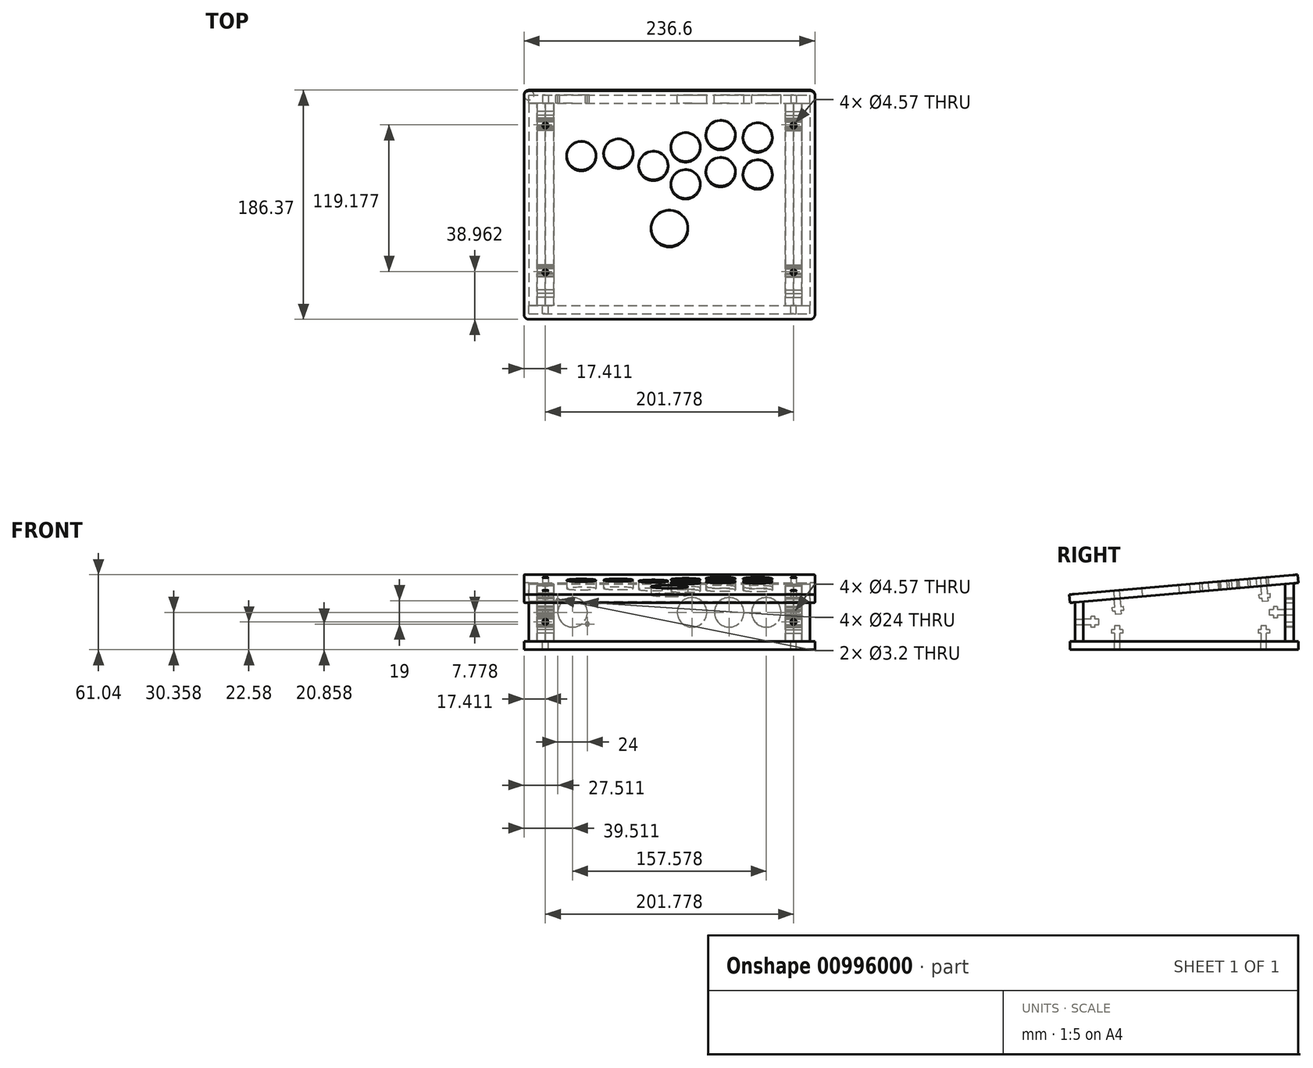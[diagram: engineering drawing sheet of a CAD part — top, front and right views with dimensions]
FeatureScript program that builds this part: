
annotation { "Feature Type Name" : "Feature", "Feature Type Description" : "" }
export const myFeature = defineFeature(function(context is Context, id is Id, definition is map)
    precondition{}
    {
        {
            var Q0;
            Q0=qCreatedBy(makeId("Right.planeOp"),FACE);
            var sketch = newSketch(context, id + "F0", { "sketchPlane" : qUnion([Q0])});
            skLineSegment(sketch, "E0", {"start": v(-88.9, -15.88) * mm, "end": v(88.9, -15.88) * mm});
            skLineSegment(sketch, "E1", {"start": v(88.9, -15.88) * mm, "end": v(88.9, 31.43) * mm});
            skLineSegment(sketch, "E2", {"start": v(88.9, 31.43) * mm, "end": v(-88.9, 15.87) * mm});
            skLineSegment(sketch, "E3", {"start": v(-88.9, 15.88) * mm, "end": v(-88.9, -15.87) * mm});
            skLineSegment(sketch, "E4", {"start": v(82.2, 30.84) * mm, "end": v(82.2, -15.88) * mm});
            skLineSegment(sketch, "E5", {"start": v(-82.2, 16.46) * mm, "end": v(-82.2, -15.88) * mm});
            skLineSegment(sketch, "E6", {"start": v(66.95, -15.88) * mm, "end": v(66.95, -3.17) * mm});
            skLineSegment(sketch, "E7", {"start": v(66.95, -3.17) * mm, "end": v(62.38, -3.17) * mm});
            skLineSegment(sketch, "E8", {"start": v(62.38, -3.17) * mm, "end": v(62.38, -15.88) * mm});
            skLineSegment(sketch, "E9", {"start": v(-52.22, -15.88) * mm, "end": v(-52.22, -3.17) * mm});
            skLineSegment(sketch, "E10", {"start": v(-52.22, -3.17) * mm, "end": v(-56.8, -3.17) * mm});
            skLineSegment(sketch, "E11", {"start": v(-56.8, -3.17) * mm, "end": v(-56.8, -15.88) * mm});
            skLineSegment(sketch, "E12", {"start": v(67.01, 29.52) * mm, "end": v(68.12, 16.86) * mm});
            skLineSegment(sketch, "E13", {"start": v(68.12, 16.86) * mm, "end": v(63.56, 16.47) * mm});
            skLineSegment(sketch, "E14", {"start": v(63.56, 16.47) * mm, "end": v(62.46, 29.12) * mm});
            skLineSegment(sketch, "E15", {"start": v(-52.34, 19.07) * mm, "end": v(-51.23, 6.42) * mm});
            skLineSegment(sketch, "E16", {"start": v(-51.23, 6.42) * mm, "end": v(-55.78, 6.02) * mm});
            skLineSegment(sketch, "E17", {"start": v(-55.78, 6.02) * mm, "end": v(-56.9, 18.68) * mm});
            skLineSegment(sketch, "E18", {"start": v(82.2, 5.5) * mm, "end": v(69.5, 5.5) * mm});
            skLineSegment(sketch, "E19", {"start": v(69.5, 5.5) * mm, "end": v(69.5, 10.06) * mm});
            skLineSegment(sketch, "E20", {"start": v(69.5, 10.06) * mm, "end": v(82.2, 10.06) * mm});
            skLineSegment(sketch, "E21", {"start": v(-82.2, -2.29) * mm, "end": v(-69.5, -2.29) * mm});
            skLineSegment(sketch, "E22", {"start": v(-69.5, -2.29) * mm, "end": v(-69.5, 2.29) * mm});
            skLineSegment(sketch, "E23", {"start": v(-69.5, 2.29) * mm, "end": v(-82.2, 2.29) * mm});
            skPoint(sketch, "E24", {"position": v(-69.5, 0) * mm});
            skPoint(sketch, "E25", {"position": v(69.5, 7.78) * mm});
            skPoint(sketch, "E26", {"position": v(88.9, 7.78) * mm});
            skPoint(sketch, "E27", {"position": v(-88.9, 0) * mm});
            skLineSegment(sketch, "E28.bottom", {"start": v(69.24, -6.22) * mm, "end": v(60.1, -6.22) * mm});
            skLineSegment(sketch, "E28.top", {"start": v(69.24, -9.27) * mm, "end": v(60.1, -9.27) * mm});
            skLineSegment(sketch, "E28.left", {"start": v(69.24, -6.22) * mm, "end": v(69.24, -9.27) * mm});
            skLineSegment(sketch, "E28.right", {"start": v(60.1, -6.22) * mm, "end": v(60.1, -9.27) * mm});
            skLineSegment(sketch, "E29.bottom", {"start": v(-49.94, -6.22) * mm, "end": v(-59.08, -6.22) * mm});
            skLineSegment(sketch, "E29.top", {"start": v(-49.94, -9.27) * mm, "end": v(-59.08, -9.27) * mm});
            skLineSegment(sketch, "E29.left", {"start": v(-49.94, -6.22) * mm, "end": v(-49.94, -9.27) * mm});
            skLineSegment(sketch, "E29.right", {"start": v(-59.08, -6.22) * mm, "end": v(-59.08, -9.27) * mm});
            skLineSegment(sketch, "E30.bottom", {"start": v(-72.54, -4.57) * mm, "end": v(-75.6, -4.57) * mm});
            skLineSegment(sketch, "E30.top", {"start": v(-72.54, 4.57) * mm, "end": v(-75.6, 4.57) * mm});
            skLineSegment(sketch, "E30.left", {"start": v(-72.54, -4.57) * mm, "end": v(-72.54, 4.57) * mm});
            skLineSegment(sketch, "E30.right", {"start": v(-75.6, -4.57) * mm, "end": v(-75.6, 4.57) * mm});
            skLineSegment(sketch, "E31.bottom", {"start": v(-58.33, 8.86) * mm, "end": v(-49.22, 9.66) * mm});
            skLineSegment(sketch, "E31.top", {"start": v(-58.6, 11.9) * mm, "end": v(-49.48, 12.7) * mm});
            skLineSegment(sketch, "E31.left", {"start": v(-58.33, 8.86) * mm, "end": v(-58.6, 11.9) * mm});
            skLineSegment(sketch, "E31.right", {"start": v(-49.22, 9.66) * mm, "end": v(-49.48, 12.7) * mm});
            skLineSegment(sketch, "E32.bottom", {"start": v(61.02, 19.3) * mm, "end": v(70.13, 20.1) * mm});
            skLineSegment(sketch, "E32.top", {"start": v(60.76, 22.34) * mm, "end": v(69.87, 23.14) * mm});
            skLineSegment(sketch, "E32.left", {"start": v(61.02, 19.3) * mm, "end": v(60.76, 22.34) * mm});
            skLineSegment(sketch, "E32.right", {"start": v(70.13, 20.1) * mm, "end": v(69.87, 23.14) * mm});
            skLineSegment(sketch, "E33.bottom", {"start": v(75.6, 12.35) * mm, "end": v(72.54, 12.35) * mm});
            skLineSegment(sketch, "E33.top", {"start": v(75.6, 3.2) * mm, "end": v(72.54, 3.2) * mm});
            skLineSegment(sketch, "E33.left", {"start": v(75.6, 12.35) * mm, "end": v(75.6, 3.2) * mm});
            skLineSegment(sketch, "E33.right", {"start": v(72.54, 12.35) * mm, "end": v(72.54, 3.2) * mm});
            skLineSegment(sketch, "E34", {"start": v(66.95, -3.17) * mm, "end": v(69.24, -6.22) * mm, "construction": true});
            skLineSegment(sketch, "E35", {"start": v(62.38, -3.17) * mm, "end": v(60.1, -6.22) * mm, "construction": true});
            skLineSegment(sketch, "E36", {"start": v(72.54, 3.2) * mm, "end": v(69.5, 5.5) * mm, "construction": true});
            skLineSegment(sketch, "E37", {"start": v(69.5, 10.06) * mm, "end": v(72.54, 12.35) * mm, "construction": true});
            skLineSegment(sketch, "E38", {"start": v(68.12, 16.86) * mm, "end": v(70.13, 20.1) * mm, "construction": true});
            skLineSegment(sketch, "E39", {"start": v(63.56, 16.47) * mm, "end": v(61.02, 19.3) * mm, "construction": true});
            skLineSegment(sketch, "E40", {"start": v(-51.23, 6.42) * mm, "end": v(-49.22, 9.66) * mm, "construction": true});
            skLineSegment(sketch, "E41", {"start": v(-55.78, 6.02) * mm, "end": v(-58.33, 8.86) * mm, "construction": true});
            skLineSegment(sketch, "E42", {"start": v(-69.5, 2.29) * mm, "end": v(-72.54, 4.57) * mm, "construction": true});
            skLineSegment(sketch, "E43", {"start": v(-69.5, -2.29) * mm, "end": v(-72.54, -4.57) * mm, "construction": true});
            skLineSegment(sketch, "E44", {"start": v(-52.22, -3.17) * mm, "end": v(-49.94, -6.22) * mm, "construction": true});
            skLineSegment(sketch, "E45", {"start": v(-56.8, -3.17) * mm, "end": v(-59.08, -6.22) * mm, "construction": true});
            skLineSegment(sketch, "E46", {"start": v(-88.9, 15.88) * mm, "end": v(88.9, 15.87) * mm, "construction": true});
            skSolve(sketch);
        }
        {
            var Q0;
            {var subQ14=sQuery(id+"F0.wireOp",EDGE,"E4");Q0=makeQuery(id+"F0.imprint","IMPRINT",FACE,{"disambiguationData":[TD([[makeQuery(id+"F0.imprint","IMPRINT",EDGE,{"derivedFrom":subQ14}),-1.0]])]});}
            var Q1;
            {var subQ0=sQuery(id+"F0.wireOp",EDGE,"dgdBLiuN-7DTV-gzHf-jHKZ-Ratlxp1D41V1.bottom");Q1=makeQuery(id+"F0.imprint","IMPRINT",FACE,{"disambiguationData":[TD([[makeQuery(id+"F0.imprint","IMPRINT",EDGE,{"derivedFrom":subQ0}),1.0]])]});}
            var Q2;
            {var subQ0=sQuery(id+"F0.wireOp",EDGE,"dgdBLiuN-7DTV-gzHf-jHKZ-Ratlxp1D41V1.top");Q2=makeQuery(id+"F0.imprint","IMPRINT",FACE,{"disambiguationData":[TD([[makeQuery(id+"F0.imprint","IMPRINT",EDGE,{"derivedFrom":subQ0}),-1.0]])]});}
            var Q3;
            {var subQ5=sQuery(id+"F0.wireOp",EDGE,"fHmdqq7Y-QNzh-l0Eo-8w8f-Dmk2epEtvhAU.left");Q3=makeQuery(id+"F0.imprint","IMPRINT",FACE,{"disambiguationData":[TD([[makeQuery(id+"F0.imprint","IMPRINT",EDGE,{"derivedFrom":subQ5}),-1.0]])]});}
            var Q4;
            {var subQ5=sQuery(id+"F0.wireOp",EDGE,"fHmdqq7Y-QNzh-l0Eo-8w8f-Dmk2epEtvhAU.right");Q4=makeQuery(id+"F0.imprint","IMPRINT",FACE,{"disambiguationData":[TD([[makeQuery(id+"F0.imprint","IMPRINT",EDGE,{"derivedFrom":subQ5}),1.0]])]});}
            var Q5;
            {var subQ0=sQuery(id+"F0.wireOp",EDGE,"fHmdqq7Y-QNzh-l0Eo-8w8f-Dmk2epEtvhAU.bottom");var subQ1=sQuery(id+"F0.wireOp",EDGE,"dgdBLiuN-7DTV-gzHf-jHKZ-Ratlxp1D41V1.left");var subQ2=makeQuery(id+"F0.imprint","INTERSECT",VERTEX,{"derivedFrom":[subQ1,subQ0]});Q5=makeQuery(id+"F0.imprint","IMPRINT",FACE,{"disambiguationData":[TD([[makeQuery(id+"F0.imprint","IMPRINT",EDGE,{"disambiguationData":[TD([[subQ2,-1.0]])],"derivedFrom":subQ1}),-1.0]])]});}
            var Q6;
            {var subQ0=sQuery(id+"F0.wireOp",EDGE,"E12");Q6=makeQuery(id+"F0.imprint","IMPRINT",FACE,{"disambiguationData":[TD([[makeQuery(id+"F0.imprint","IMPRINT",EDGE,{"derivedFrom":subQ0}),-1.0]])]});}
            var Q7;
            {var subQ0=sQuery(id+"F0.wireOp",EDGE,"E15");Q7=makeQuery(id+"F0.imprint","IMPRINT",FACE,{"disambiguationData":[TD([[makeQuery(id+"F0.imprint","IMPRINT",EDGE,{"derivedFrom":subQ0}),-1.0]])]});}
            var Q8;
            {var subQ0=sQuery(id+"F0.wireOp",EDGE,"E21");Q8=makeQuery(id+"F0.imprint","IMPRINT",FACE,{"disambiguationData":[TD([[makeQuery(id+"F0.imprint","IMPRINT",EDGE,{"derivedFrom":subQ0}),1.0]])]});}
            var Q9;
            {var subQ0=sQuery(id+"F0.wireOp",EDGE,"E9");Q9=makeQuery(id+"F0.imprint","IMPRINT",FACE,{"disambiguationData":[TD([[makeQuery(id+"F0.imprint","IMPRINT",EDGE,{"derivedFrom":subQ0}),1.0]])]});}
            var Q10;
            {var subQ0=sQuery(id+"F0.wireOp",EDGE,"E6");Q10=makeQuery(id+"F0.imprint","IMPRINT",FACE,{"disambiguationData":[TD([[makeQuery(id+"F0.imprint","IMPRINT",EDGE,{"derivedFrom":subQ0}),1.0]])]});}
            var Q11;
            {var subQ0=sQuery(id+"F0.wireOp",EDGE,"E18");Q11=makeQuery(id+"F0.imprint","IMPRINT",FACE,{"disambiguationData":[TD([[makeQuery(id+"F0.imprint","IMPRINT",EDGE,{"derivedFrom":subQ0}),-1.0]])]});}
            var Q12;
            {var subQ5=sQuery(id+"F0.wireOp",EDGE,"E32.left");Q12=makeQuery(id+"F0.imprint","IMPRINT",FACE,{"disambiguationData":[TD([[makeQuery(id+"F0.imprint","IMPRINT",EDGE,{"derivedFrom":subQ5}),-1.0]])]});}
            var Q13;
            {var subQ5=sQuery(id+"F0.wireOp",EDGE,"E32.right");Q13=makeQuery(id+"F0.imprint","IMPRINT",FACE,{"disambiguationData":[TD([[makeQuery(id+"F0.imprint","IMPRINT",EDGE,{"derivedFrom":subQ5}),1.0]])]});}
            var Q14;
            {var subQ5=sQuery(id+"F0.wireOp",EDGE,"E33.top");Q14=makeQuery(id+"F0.imprint","IMPRINT",FACE,{"disambiguationData":[TD([[makeQuery(id+"F0.imprint","IMPRINT",EDGE,{"derivedFrom":subQ5}),-1.0]])]});}
            var Q15;
            {var subQ5=sQuery(id+"F0.wireOp",EDGE,"E33.bottom");Q15=makeQuery(id+"F0.imprint","IMPRINT",FACE,{"disambiguationData":[TD([[makeQuery(id+"F0.imprint","IMPRINT",EDGE,{"derivedFrom":subQ5}),1.0]])]});}
            var Q16;
            {var subQ5=sQuery(id+"F0.wireOp",EDGE,"E28.left");Q16=makeQuery(id+"F0.imprint","IMPRINT",FACE,{"disambiguationData":[TD([[makeQuery(id+"F0.imprint","IMPRINT",EDGE,{"derivedFrom":subQ5}),-1.0]])]});}
            var Q17;
            {var subQ5=sQuery(id+"F0.wireOp",EDGE,"E28.right");Q17=makeQuery(id+"F0.imprint","IMPRINT",FACE,{"disambiguationData":[TD([[makeQuery(id+"F0.imprint","IMPRINT",EDGE,{"derivedFrom":subQ5}),1.0]])]});}
            var Q18;
            {var subQ5=sQuery(id+"F0.wireOp",EDGE,"E29.left");Q18=makeQuery(id+"F0.imprint","IMPRINT",FACE,{"disambiguationData":[TD([[makeQuery(id+"F0.imprint","IMPRINT",EDGE,{"derivedFrom":subQ5}),-1.0]])]});}
            var Q19;
            {var subQ5=sQuery(id+"F0.wireOp",EDGE,"E29.right");Q19=makeQuery(id+"F0.imprint","IMPRINT",FACE,{"disambiguationData":[TD([[makeQuery(id+"F0.imprint","IMPRINT",EDGE,{"derivedFrom":subQ5}),1.0]])]});}
            var Q20;
            {var subQ5=sQuery(id+"F0.wireOp",EDGE,"E30.bottom");Q20=makeQuery(id+"F0.imprint","IMPRINT",FACE,{"disambiguationData":[TD([[makeQuery(id+"F0.imprint","IMPRINT",EDGE,{"derivedFrom":subQ5}),-1.0]])]});}
            var Q21;
            {var subQ5=sQuery(id+"F0.wireOp",EDGE,"E30.top");Q21=makeQuery(id+"F0.imprint","IMPRINT",FACE,{"disambiguationData":[TD([[makeQuery(id+"F0.imprint","IMPRINT",EDGE,{"derivedFrom":subQ5}),1.0]])]});}
            var Q22;
            {var subQ5=sQuery(id+"F0.wireOp",EDGE,"E31.left");Q22=makeQuery(id+"F0.imprint","IMPRINT",FACE,{"disambiguationData":[TD([[makeQuery(id+"F0.imprint","IMPRINT",EDGE,{"derivedFrom":subQ5}),-1.0]])]});}
            var Q23;
            {var subQ5=sQuery(id+"F0.wireOp",EDGE,"E31.right");Q23=makeQuery(id+"F0.imprint","IMPRINT",FACE,{"disambiguationData":[TD([[makeQuery(id+"F0.imprint","IMPRINT",EDGE,{"derivedFrom":subQ5}),1.0]])]});}
            var Q24;
            {var subQ0=sQuery(id+"F0.wireOp",EDGE,"UAsRLKdk-vdFN-tKB4-pKpE-Und0eIql7xDi");Q24=makeQuery(id+"F0.imprint","IMPRINT",FACE,{"disambiguationData":[TD([[makeQuery(id+"F0.imprint","IMPRINT",EDGE,{"derivedFrom":subQ0}),1.0]])]});}
            extrude(context, id + "F1", {"entities" : qUnion([Q0, Q1, Q2, Q3, Q4, Q5, Q6, Q7, Q8, Q9, Q10, Q11, Q12, Q13, Q14, Q15, Q16, Q17, Q18, Q19, Q20, Q21, Q22, Q23, Q24]), "oppositeDirection" : true, "depth" : 6.7 * mm, "offsetDistance" : 25.4 * mm});
        }
        {
            var Q0;
            {var subQ14=sQuery(id+"F0.wireOp",EDGE,"E4");Q0=makeQuery(id+"F0.imprint","IMPRINT",FACE,{"disambiguationData":[TD([[makeQuery(id+"F0.imprint","IMPRINT",EDGE,{"derivedFrom":subQ14}),-1.0]])]});}
            extrude(context, id + "F2", {"entities" : qUnion([Q0]), "oppositeDirection" : true, "depth" : 6.7 * mm, "offsetDistance" : 25.4 * mm});
        }
        {
            var Q0;
            Q0=makeQuery(id+"F2.opExtrude","SWEPT_BODY",BODY,{"disambiguationData":[OSD([sQuery(id+"F0.wireOp",EDGE,"E0"),sQuery(id+"F0.wireOp",EDGE,"E2"),sQuery(id+"F0.wireOp",EDGE,"E4"),sQuery(id+"F0.wireOp",EDGE,"E5"),sQuery(id+"F0.wireOp",EDGE,"E6"),sQuery(id+"F0.wireOp",EDGE,"E7"),sQuery(id+"F0.wireOp",EDGE,"E8"),sQuery(id+"F0.wireOp",EDGE,"E9"),sQuery(id+"F0.wireOp",EDGE,"E10"),sQuery(id+"F0.wireOp",EDGE,"E11"),sQuery(id+"F0.wireOp",EDGE,"E12"),sQuery(id+"F0.wireOp",EDGE,"E13"),sQuery(id+"F0.wireOp",EDGE,"E14"),sQuery(id+"F0.wireOp",EDGE,"E15"),sQuery(id+"F0.wireOp",EDGE,"E16"),sQuery(id+"F0.wireOp",EDGE,"E17"),sQuery(id+"F0.wireOp",EDGE,"E18"),sQuery(id+"F0.wireOp",EDGE,"E19"),sQuery(id+"F0.wireOp",EDGE,"E20"),sQuery(id+"F0.wireOp",EDGE,"E21"),sQuery(id+"F0.wireOp",EDGE,"E22"),sQuery(id+"F0.wireOp",EDGE,"E23"),sQuery(id+"F0.wireOp",EDGE,"E28.bottom"),sQuery(id+"F0.wireOp",EDGE,"E28.top"),sQuery(id+"F0.wireOp",EDGE,"E28.left"),sQuery(id+"F0.wireOp",EDGE,"E28.right"),sQuery(id+"F0.wireOp",EDGE,"E29.bottom"),sQuery(id+"F0.wireOp",EDGE,"E29.top"),sQuery(id+"F0.wireOp",EDGE,"E29.left"),sQuery(id+"F0.wireOp",EDGE,"E29.right"),sQuery(id+"F0.wireOp",EDGE,"E30.bottom"),sQuery(id+"F0.wireOp",EDGE,"E30.top"),sQuery(id+"F0.wireOp",EDGE,"E30.left"),sQuery(id+"F0.wireOp",EDGE,"E30.right"),sQuery(id+"F0.wireOp",EDGE,"E31.bottom"),sQuery(id+"F0.wireOp",EDGE,"E31.top"),sQuery(id+"F0.wireOp",EDGE,"E31.left"),sQuery(id+"F0.wireOp",EDGE,"E31.right"),sQuery(id+"F0.wireOp",EDGE,"E32.bottom"),sQuery(id+"F0.wireOp",EDGE,"E32.top"),sQuery(id+"F0.wireOp",EDGE,"E32.left"),sQuery(id+"F0.wireOp",EDGE,"E32.right"),sQuery(id+"F0.wireOp",EDGE,"E33.bottom"),sQuery(id+"F0.wireOp",EDGE,"E33.top"),sQuery(id+"F0.wireOp",EDGE,"E33.left"),sQuery(id+"F0.wireOp",EDGE,"E33.right")])]});
            var Q1;
            Q1=makeQuery(id+"F1.opExtrude","SWEPT_EDGE",EDGE,{"disambiguationData":[OSD([sQuery(id+"F0.wireOp",EDGE,"E2"),sQuery(id+"F0.wireOp",EDGE,"E5")])]});
            transform(context, id + "F3", {"entities" : qUnion([Q0]), "transformType" : TransformType.TRANSLATION_ENTITY, "oppositeDirectionEntity" : true, "transformLine" : qUnion([Q1]), "makeCopy" : false});
        }
        {
            var Q0;
            Q0=makeQuery(id+"F2.opExtrude","CAP_FACE",FACE,{"disambiguationData":[OSD([sQuery(id+"F0.wireOp",EDGE,"E0"),sQuery(id+"F0.wireOp",EDGE,"E2"),sQuery(id+"F0.wireOp",EDGE,"E4"),sQuery(id+"F0.wireOp",EDGE,"E5"),sQuery(id+"F0.wireOp",EDGE,"E6"),sQuery(id+"F0.wireOp",EDGE,"E7"),sQuery(id+"F0.wireOp",EDGE,"E8"),sQuery(id+"F0.wireOp",EDGE,"E9"),sQuery(id+"F0.wireOp",EDGE,"E10"),sQuery(id+"F0.wireOp",EDGE,"E11"),sQuery(id+"F0.wireOp",EDGE,"E12"),sQuery(id+"F0.wireOp",EDGE,"E13"),sQuery(id+"F0.wireOp",EDGE,"E14"),sQuery(id+"F0.wireOp",EDGE,"E15"),sQuery(id+"F0.wireOp",EDGE,"E16"),sQuery(id+"F0.wireOp",EDGE,"E17"),sQuery(id+"F0.wireOp",EDGE,"E18"),sQuery(id+"F0.wireOp",EDGE,"E19"),sQuery(id+"F0.wireOp",EDGE,"E20"),sQuery(id+"F0.wireOp",EDGE,"E21"),sQuery(id+"F0.wireOp",EDGE,"E22"),sQuery(id+"F0.wireOp",EDGE,"E23"),sQuery(id+"F0.wireOp",EDGE,"E28.bottom"),sQuery(id+"F0.wireOp",EDGE,"E28.top"),sQuery(id+"F0.wireOp",EDGE,"E28.left"),sQuery(id+"F0.wireOp",EDGE,"E28.right"),sQuery(id+"F0.wireOp",EDGE,"E29.bottom"),sQuery(id+"F0.wireOp",EDGE,"E29.top"),sQuery(id+"F0.wireOp",EDGE,"E29.left"),sQuery(id+"F0.wireOp",EDGE,"E29.right"),sQuery(id+"F0.wireOp",EDGE,"E30.bottom"),sQuery(id+"F0.wireOp",EDGE,"E30.top"),sQuery(id+"F0.wireOp",EDGE,"E30.left"),sQuery(id+"F0.wireOp",EDGE,"E30.right"),sQuery(id+"F0.wireOp",EDGE,"E31.bottom"),sQuery(id+"F0.wireOp",EDGE,"E31.top"),sQuery(id+"F0.wireOp",EDGE,"E31.left"),sQuery(id+"F0.wireOp",EDGE,"E31.right"),sQuery(id+"F0.wireOp",EDGE,"E32.bottom"),sQuery(id+"F0.wireOp",EDGE,"E32.top"),sQuery(id+"F0.wireOp",EDGE,"E32.left"),sQuery(id+"F0.wireOp",EDGE,"E32.right"),sQuery(id+"F0.wireOp",EDGE,"E33.bottom"),sQuery(id+"F0.wireOp",EDGE,"E33.top"),sQuery(id+"F0.wireOp",EDGE,"E33.left"),sQuery(id+"F0.wireOp",EDGE,"E33.right")])],"isStart":false});
            extrude(context, id + "F4", {"entities" : qUnion([Q0]), "depth" : 6.7 * mm, "offsetDistance" : 25.4 * mm});
        }
        {
            var Q0;
            Q0=makeQuery(id+"F1.opExtrude","SWEPT_BODY",BODY,{"disambiguationData":[OSD([sQuery(id+"F0.wireOp",EDGE,"E0"),sQuery(id+"F0.wireOp",EDGE,"E2"),sQuery(id+"F0.wireOp",EDGE,"E4"),sQuery(id+"F0.wireOp",EDGE,"E5"),sQuery(id+"F0.wireOp",EDGE,"dgdBLiuN-7DTV-gzHf-jHKZ-Ratlxp1D41V1.bottom")])]});
            var Q1;
            Q1=makeQuery(id+"F2.opExtrude","SWEPT_BODY",BODY,{"disambiguationData":[OSD([sQuery(id+"F0.wireOp",EDGE,"E0"),sQuery(id+"F0.wireOp",EDGE,"E2"),sQuery(id+"F0.wireOp",EDGE,"E4"),sQuery(id+"F0.wireOp",EDGE,"E5"),sQuery(id+"F0.wireOp",EDGE,"dgdBLiuN-7DTV-gzHf-jHKZ-Ratlxp1D41V1.top"),sQuery(id+"F0.wireOp",EDGE,"dgdBLiuN-7DTV-gzHf-jHKZ-Ratlxp1D41V1.left"),sQuery(id+"F0.wireOp",EDGE,"dgdBLiuN-7DTV-gzHf-jHKZ-Ratlxp1D41V1.right"),sQuery(id+"F0.wireOp",EDGE,"fHmdqq7Y-QNzh-l0Eo-8w8f-Dmk2epEtvhAU.bottom"),sQuery(id+"F0.wireOp",EDGE,"fHmdqq7Y-QNzh-l0Eo-8w8f-Dmk2epEtvhAU.top"),sQuery(id+"F0.wireOp",EDGE,"fHmdqq7Y-QNzh-l0Eo-8w8f-Dmk2epEtvhAU.left"),sQuery(id+"F0.wireOp",EDGE,"fHmdqq7Y-QNzh-l0Eo-8w8f-Dmk2epEtvhAU.right")])]});
            var Q2;
            Q2=makeQuery(id+"F4.opExtrude","SWEPT_BODY",BODY,{"disambiguationData":[OSD([sQuery(id+"F0.wireOp",EDGE,"E0"),sQuery(id+"F0.wireOp",EDGE,"E2"),sQuery(id+"F0.wireOp",EDGE,"E4"),sQuery(id+"F0.wireOp",EDGE,"E5"),sQuery(id+"F0.wireOp",EDGE,"E6"),sQuery(id+"F0.wireOp",EDGE,"E7"),sQuery(id+"F0.wireOp",EDGE,"E8"),sQuery(id+"F0.wireOp",EDGE,"E9"),sQuery(id+"F0.wireOp",EDGE,"E10"),sQuery(id+"F0.wireOp",EDGE,"E11"),sQuery(id+"F0.wireOp",EDGE,"E12"),sQuery(id+"F0.wireOp",EDGE,"E13"),sQuery(id+"F0.wireOp",EDGE,"E14"),sQuery(id+"F0.wireOp",EDGE,"E15"),sQuery(id+"F0.wireOp",EDGE,"E16"),sQuery(id+"F0.wireOp",EDGE,"E17"),sQuery(id+"F0.wireOp",EDGE,"E18"),sQuery(id+"F0.wireOp",EDGE,"E19"),sQuery(id+"F0.wireOp",EDGE,"E20"),sQuery(id+"F0.wireOp",EDGE,"E21"),sQuery(id+"F0.wireOp",EDGE,"E22"),sQuery(id+"F0.wireOp",EDGE,"E23"),sQuery(id+"F0.wireOp",EDGE,"E28.bottom"),sQuery(id+"F0.wireOp",EDGE,"E28.top"),sQuery(id+"F0.wireOp",EDGE,"E28.left"),sQuery(id+"F0.wireOp",EDGE,"E28.right"),sQuery(id+"F0.wireOp",EDGE,"E29.bottom"),sQuery(id+"F0.wireOp",EDGE,"E29.top"),sQuery(id+"F0.wireOp",EDGE,"E29.left"),sQuery(id+"F0.wireOp",EDGE,"E29.right"),sQuery(id+"F0.wireOp",EDGE,"E30.bottom"),sQuery(id+"F0.wireOp",EDGE,"E30.top"),sQuery(id+"F0.wireOp",EDGE,"E30.left"),sQuery(id+"F0.wireOp",EDGE,"E30.right"),sQuery(id+"F0.wireOp",EDGE,"E31.bottom"),sQuery(id+"F0.wireOp",EDGE,"E31.top"),sQuery(id+"F0.wireOp",EDGE,"E31.left"),sQuery(id+"F0.wireOp",EDGE,"E31.right"),sQuery(id+"F0.wireOp",EDGE,"E32.bottom"),sQuery(id+"F0.wireOp",EDGE,"E32.top"),sQuery(id+"F0.wireOp",EDGE,"E32.left"),sQuery(id+"F0.wireOp",EDGE,"E32.right"),sQuery(id+"F0.wireOp",EDGE,"E33.bottom"),sQuery(id+"F0.wireOp",EDGE,"E33.top"),sQuery(id+"F0.wireOp",EDGE,"E33.left"),sQuery(id+"F0.wireOp",EDGE,"E33.right")])]});
            var Q3;
            Q3=qCreatedBy(makeId("Right.planeOp"),FACE);
            mirror(context, id + "F5", {"entities" : qUnion([Q0, Q1, Q2]), "mirrorPlane" : qUnion([Q3])});
        }
        {
            var Q0;
            Q0=makeQuery(id+"F5.opPattern","COPY",BODY,{"derivedFrom":makeQuery(id+"F1.opExtrude","SWEPT_BODY",BODY,{"disambiguationData":[OSD([sQuery(id+"F0.wireOp",EDGE,"E0"),sQuery(id+"F0.wireOp",EDGE,"E2"),sQuery(id+"F0.wireOp",EDGE,"E4"),sQuery(id+"F0.wireOp",EDGE,"E5")])]}),"instanceName":"1"});
            var Q1;
            Q1=makeQuery(id+"F5.opPattern","COPY",BODY,{"derivedFrom":makeQuery(id+"F2.opExtrude","SWEPT_BODY",BODY,{"disambiguationData":[OSD([sQuery(id+"F0.wireOp",EDGE,"E0"),sQuery(id+"F0.wireOp",EDGE,"E2"),sQuery(id+"F0.wireOp",EDGE,"E4"),sQuery(id+"F0.wireOp",EDGE,"E5"),sQuery(id+"F0.wireOp",EDGE,"E6"),sQuery(id+"F0.wireOp",EDGE,"E7"),sQuery(id+"F0.wireOp",EDGE,"E8"),sQuery(id+"F0.wireOp",EDGE,"E9"),sQuery(id+"F0.wireOp",EDGE,"E10"),sQuery(id+"F0.wireOp",EDGE,"E11"),sQuery(id+"F0.wireOp",EDGE,"E12"),sQuery(id+"F0.wireOp",EDGE,"E13"),sQuery(id+"F0.wireOp",EDGE,"E14"),sQuery(id+"F0.wireOp",EDGE,"E15"),sQuery(id+"F0.wireOp",EDGE,"E16"),sQuery(id+"F0.wireOp",EDGE,"E17"),sQuery(id+"F0.wireOp",EDGE,"E18"),sQuery(id+"F0.wireOp",EDGE,"E19"),sQuery(id+"F0.wireOp",EDGE,"E20"),sQuery(id+"F0.wireOp",EDGE,"E21"),sQuery(id+"F0.wireOp",EDGE,"E22"),sQuery(id+"F0.wireOp",EDGE,"E23"),sQuery(id+"F0.wireOp",EDGE,"E28.bottom"),sQuery(id+"F0.wireOp",EDGE,"E28.top"),sQuery(id+"F0.wireOp",EDGE,"E28.left"),sQuery(id+"F0.wireOp",EDGE,"E28.right"),sQuery(id+"F0.wireOp",EDGE,"E29.bottom"),sQuery(id+"F0.wireOp",EDGE,"E29.top"),sQuery(id+"F0.wireOp",EDGE,"E29.left"),sQuery(id+"F0.wireOp",EDGE,"E29.right"),sQuery(id+"F0.wireOp",EDGE,"E30.bottom"),sQuery(id+"F0.wireOp",EDGE,"E30.top"),sQuery(id+"F0.wireOp",EDGE,"E30.left"),sQuery(id+"F0.wireOp",EDGE,"E30.right"),sQuery(id+"F0.wireOp",EDGE,"E31.bottom"),sQuery(id+"F0.wireOp",EDGE,"E31.top"),sQuery(id+"F0.wireOp",EDGE,"E31.left"),sQuery(id+"F0.wireOp",EDGE,"E31.right"),sQuery(id+"F0.wireOp",EDGE,"E32.bottom"),sQuery(id+"F0.wireOp",EDGE,"E32.top"),sQuery(id+"F0.wireOp",EDGE,"E32.left"),sQuery(id+"F0.wireOp",EDGE,"E32.right"),sQuery(id+"F0.wireOp",EDGE,"E33.bottom"),sQuery(id+"F0.wireOp",EDGE,"E33.top"),sQuery(id+"F0.wireOp",EDGE,"E33.left"),sQuery(id+"F0.wireOp",EDGE,"E33.right")])]}),"instanceName":"1"});
            var Q2;
            Q2=makeQuery(id+"F5.opPattern","COPY",BODY,{"derivedFrom":makeQuery(id+"F4.opExtrude","SWEPT_BODY",BODY,{"disambiguationData":[OSD([sQuery(id+"F0.wireOp",EDGE,"E0"),sQuery(id+"F0.wireOp",EDGE,"E2"),sQuery(id+"F0.wireOp",EDGE,"E4"),sQuery(id+"F0.wireOp",EDGE,"E5"),sQuery(id+"F0.wireOp",EDGE,"E6"),sQuery(id+"F0.wireOp",EDGE,"E7"),sQuery(id+"F0.wireOp",EDGE,"E8"),sQuery(id+"F0.wireOp",EDGE,"E9"),sQuery(id+"F0.wireOp",EDGE,"E10"),sQuery(id+"F0.wireOp",EDGE,"E11"),sQuery(id+"F0.wireOp",EDGE,"E12"),sQuery(id+"F0.wireOp",EDGE,"E13"),sQuery(id+"F0.wireOp",EDGE,"E14"),sQuery(id+"F0.wireOp",EDGE,"E15"),sQuery(id+"F0.wireOp",EDGE,"E16"),sQuery(id+"F0.wireOp",EDGE,"E17"),sQuery(id+"F0.wireOp",EDGE,"E18"),sQuery(id+"F0.wireOp",EDGE,"E19"),sQuery(id+"F0.wireOp",EDGE,"E20"),sQuery(id+"F0.wireOp",EDGE,"E21"),sQuery(id+"F0.wireOp",EDGE,"E22"),sQuery(id+"F0.wireOp",EDGE,"E23"),sQuery(id+"F0.wireOp",EDGE,"E28.bottom"),sQuery(id+"F0.wireOp",EDGE,"E28.top"),sQuery(id+"F0.wireOp",EDGE,"E28.left"),sQuery(id+"F0.wireOp",EDGE,"E28.right"),sQuery(id+"F0.wireOp",EDGE,"E29.bottom"),sQuery(id+"F0.wireOp",EDGE,"E29.top"),sQuery(id+"F0.wireOp",EDGE,"E29.left"),sQuery(id+"F0.wireOp",EDGE,"E29.right"),sQuery(id+"F0.wireOp",EDGE,"E30.bottom"),sQuery(id+"F0.wireOp",EDGE,"E30.top"),sQuery(id+"F0.wireOp",EDGE,"E30.left"),sQuery(id+"F0.wireOp",EDGE,"E30.right"),sQuery(id+"F0.wireOp",EDGE,"E31.bottom"),sQuery(id+"F0.wireOp",EDGE,"E31.top"),sQuery(id+"F0.wireOp",EDGE,"E31.left"),sQuery(id+"F0.wireOp",EDGE,"E31.right"),sQuery(id+"F0.wireOp",EDGE,"E32.bottom"),sQuery(id+"F0.wireOp",EDGE,"E32.top"),sQuery(id+"F0.wireOp",EDGE,"E32.left"),sQuery(id+"F0.wireOp",EDGE,"E32.right"),sQuery(id+"F0.wireOp",EDGE,"E33.bottom"),sQuery(id+"F0.wireOp",EDGE,"E33.top"),sQuery(id+"F0.wireOp",EDGE,"E33.left"),sQuery(id+"F0.wireOp",EDGE,"E33.right")])]}),"instanceName":"1"});
            transform(context, id + "F6", {"entities" : qUnion([Q0, Q1, Q2]), "transformType" : TransformType.TRANSLATION_3D, "dx" : -228.6 * mm, "dy" : 0 * mm, "dz" : 0 * mm, "makeCopy" : false});
        }
        {
            var Q0;
            {var subQ0=sQuery(id+"F0.wireOp",EDGE,"E3");Q0=makeQuery(id+"F0.imprint","IMPRINT",FACE,{"disambiguationData":[TD([[makeQuery(id+"F0.imprint","IMPRINT",EDGE,{"derivedFrom":subQ0}),1.0]])]});}
            var Q1;
            {var subQ0=sQuery(id+"F0.wireOp",EDGE,"E1");Q1=makeQuery(id+"F0.imprint","IMPRINT",FACE,{"disambiguationData":[TD([[makeQuery(id+"F0.imprint","IMPRINT",EDGE,{"derivedFrom":subQ0}),1.0]])]});}
            var Q2;
            Q2=makeQuery(id+"F5.opPattern","COPY",FACE,{"derivedFrom":makeQuery(id+"F1.opExtrude","CAP_FACE",FACE,{"disambiguationData":[OSD([sQuery(id+"F0.wireOp",EDGE,"E0"),sQuery(id+"F0.wireOp",EDGE,"E2"),sQuery(id+"F0.wireOp",EDGE,"E4"),sQuery(id+"F0.wireOp",EDGE,"E5")])],"isStart":true}),"instanceName":"1"});
            extrude(context, id + "F7", {"entities" : qUnion([Q0, Q1]), "endBound" : BoundingType.UP_TO_SURFACE, "oppositeDirection" : true, "depth" : 254 * mm, "endBoundEntityFace" : qUnion([Q2]), "offsetDistance" : 25.4 * mm});
        }
        {
            var Q0;
            Q0=makeQuery(id+"F7.opExtrude","SWEPT_FACE",FACE,{"disambiguationData":[OSD([sQuery(id+"F0.wireOp",EDGE,"E5")])]});
            var sketch = newSketch(context, id + "F8", { "sketchPlane" : qUnion([Q0])});
            skCircle(sketch, "E47", {"center": v(215.19, 0) * mm, "radius": 2.29 * mm});
            skCircle(sketch, "E48", {"center": v(13.41, 0) * mm, "radius": 2.29 * mm});
            skSolve(sketch);
        }
        {
            var Q0;
            Q0=makeQuery(id+"F7.opExtrude","SWEPT_FACE",FACE,{"disambiguationData":[OSD([sQuery(id+"F0.wireOp",EDGE,"E4")])]});
            var sketch = newSketch(context, id + "F9", { "sketchPlane" : qUnion([Q0])});
            skCircle(sketch, "E49", {"center": v(-215.19, 7.78) * mm, "radius": 2.29 * mm});
            skCircle(sketch, "E50", {"center": v(-13.41, 7.78) * mm, "radius": 2.29 * mm});
            skSolve(sketch);
        }
        {
            var Q0;
            Q0=qSketchRegion(id+"F8",true);
            extrude(context, id + "F10", {"entities" : qUnion([Q0]), "operationType" : NewBodyOperationType.REMOVE, "endBound" : BoundingType.UP_TO_NEXT, "oppositeDirection" : true, "depth" : 25.4 * mm, "offsetDistance" : 25.4 * mm});
        }
        {
            var Q0;
            Q0=qSketchRegion(id+"F9",true);
            extrude(context, id + "F11", {"entities" : qUnion([Q0]), "operationType" : NewBodyOperationType.REMOVE, "endBound" : BoundingType.UP_TO_NEXT, "oppositeDirection" : true, "depth" : 25.4 * mm, "offsetDistance" : 25.4 * mm});
        }
        {
            var Q0;
            Q0=makeQuery(id+"F1.opExtrude","SWEPT_FACE",FACE,{"disambiguationData":[OSD([sQuery(id+"F0.wireOp",EDGE,"E2")])]});
            var sketch = newSketch(context, id + "F12", { "sketchPlane" : qUnion([Q0])});
            skCircle(sketch, "E51", {"center": v(-114.3, -17.08) * mm, "radius": 15 * mm});
            skCircle(sketch, "E52", {"center": v(-186, 42.07) * mm, "radius": 12 * mm});
            skCircle(sketch, "E53", {"center": v(-155.87, 44.07) * mm, "radius": 12 * mm});
            skCircle(sketch, "E54", {"center": v(-127.38, 34.07) * mm, "radius": 12 * mm});
            skCircle(sketch, "E55", {"center": v(-101.22, 49.17) * mm, "radius": 12 * mm});
            skCircle(sketch, "E56", {"center": v(-72.73, 59.17) * mm, "radius": 12 * mm});
            skCircle(sketch, "E57", {"center": v(-42.6, 57.17) * mm, "radius": 12 * mm});
            skCircle(sketch, "E58", {"center": v(-101.22, 18.97) * mm, "radius": 12 * mm});
            skCircle(sketch, "E59", {"center": v(-72.73, 28.97) * mm, "radius": 12 * mm});
            skCircle(sketch, "E60", {"center": v(-42.6, 26.97) * mm, "radius": 12 * mm});
            skCircle(sketch, "E61", {"center": v(-186, 42.07) * mm, "radius": 13.6 * mm, "construction": true});
            skCircle(sketch, "E62", {"center": v(-155.87, 44.07) * mm, "radius": 13.6 * mm, "construction": true});
            skCircle(sketch, "E63", {"center": v(-127.38, 34.07) * mm, "radius": 13.6 * mm, "construction": true});
            skCircle(sketch, "E64", {"center": v(-101.22, 49.17) * mm, "radius": 13.6 * mm, "construction": true});
            skCircle(sketch, "E65", {"center": v(-72.73, 59.17) * mm, "radius": 13.6 * mm, "construction": true});
            skCircle(sketch, "E66", {"center": v(-42.6, 57.17) * mm, "radius": 13.6 * mm, "construction": true});
            skCircle(sketch, "E67", {"center": v(-101.22, 18.97) * mm, "radius": 13.6 * mm, "construction": true});
            skCircle(sketch, "E68", {"center": v(-72.73, 28.97) * mm, "radius": 13.6 * mm, "construction": true});
            skCircle(sketch, "E69", {"center": v(-42.6, 26.97) * mm, "radius": 13.6 * mm, "construction": true});
            skCircle(sketch, "E70", {"center": v(-114.3, -17.08) * mm, "radius": 16.75 * mm, "construction": true});
            skLineSegment(sketch, "E71", {"start": v(-101.22, 18.97) * mm, "end": v(-72.73, 28.97) * mm, "construction": true});
            skLineSegment(sketch, "E72", {"start": v(-72.73, 28.97) * mm, "end": v(-42.6, 26.97) * mm, "construction": true});
            skLineSegment(sketch, "E73", {"start": v(-72.73, 28.97) * mm, "end": v(-72.73, 59.17) * mm, "construction": true});
            skLineSegment(sketch, "E74", {"start": v(-42.6, 26.97) * mm, "end": v(-42.6, 57.17) * mm, "construction": true});
            skLineSegment(sketch, "E75", {"start": v(-186, 42.07) * mm, "end": v(-155.87, 44.07) * mm, "construction": true});
            skLineSegment(sketch, "E76", {"start": v(-155.87, 44.07) * mm, "end": v(-127.38, 34.07) * mm, "construction": true});
            skLineSegment(sketch, "E77", {"start": v(-127.38, 34.07) * mm, "end": v(-101.22, 18.97) * mm, "construction": true});
            skLineSegment(sketch, "E78", {"start": v(-127.38, 34.07) * mm, "end": v(-101.22, 49.17) * mm, "construction": true});
            skLineSegment(sketch, "E79", {"start": v(-101.22, 49.17) * mm, "end": v(-72.73, 59.17) * mm, "construction": true});
            skLineSegment(sketch, "E80", {"start": v(-72.73, 59.17) * mm, "end": v(-42.6, 57.17) * mm, "construction": true});
            skLineSegment(sketch, "E81", {"start": v(-101.22, 18.97) * mm, "end": v(-101.22, 49.17) * mm, "construction": true});
            skLineSegment(sketch, "E82", {"start": v(-127.38, 34.07) * mm, "end": v(-101.22, 34.07) * mm, "construction": true});
            skPoint(sketch, "E83", {"position": v(-114.3, 34.07) * mm});
            skCircle(sketch, "E84", {"center": v(-215.19, -52.76) * mm, "radius": 2.29 * mm});
            skCircle(sketch, "E85", {"center": v(-13.41, -52.76) * mm, "radius": 2.29 * mm});
            skCircle(sketch, "E86", {"center": v(-13.41, 67.04) * mm, "radius": 2.29 * mm});
            skCircle(sketch, "E87", {"center": v(-215.19, 67.04) * mm, "radius": 2.29 * mm});
            skLineSegment(sketch, "E88", {"start": v(-114.3, 91.3) * mm, "end": v(-114.3, -87.18) * mm, "construction": true});
            skLineSegment(sketch, "E89.bottom", {"start": v(-228.6, 91.3) * mm, "end": v(0, 91.3) * mm});
            skLineSegment(sketch, "E89.top", {"start": v(-228.6, -87.18) * mm, "end": v(0, -87.18) * mm});
            skLineSegment(sketch, "E89.left", {"start": v(-228.6, 91.3) * mm, "end": v(-228.6, -87.18) * mm});
            skLineSegment(sketch, "E89.right", {"start": v(0, 91.3) * mm, "end": v(0, -87.18) * mm});
            skLineSegment(sketch, "E90.0", {"start": v(-232.6, 91.3) * mm, "end": v(-232.6, -87.18) * mm});
            skLineSegment(sketch, "E90.1", {"start": v(-228.6, 95.3) * mm, "end": v(0, 95.3) * mm});
            skLineSegment(sketch, "E90.2", {"start": v(4, 91.3) * mm, "end": v(4, -87.18) * mm});
            skLineSegment(sketch, "E90.3", {"start": v(-228.6, -91.18) * mm, "end": v(0, -91.18) * mm});
            skPoint(sketch, "E91.visualSharp", {"position": v(-232.6, 95.3) * mm});
            skArc(sketch, "E91.filletArc", {"start": v(-228.6, 95.3) * mm, "mid": v(-231.43, 94.13) * mm, "end": v(-232.6, 91.3) * mm});
            skPoint(sketch, "E92.visualSharp", {"position": v(4, 95.3) * mm});
            skArc(sketch, "E92.filletArc", {"start": v(4, 91.3) * mm, "mid": v(2.83, 94.13) * mm, "end": v(0, 95.3) * mm});
            skPoint(sketch, "E93.visualSharp", {"position": v(4, -91.18) * mm});
            skArc(sketch, "E93.filletArc", {"start": v(0, -91.18) * mm, "mid": v(2.83, -90) * mm, "end": v(4, -87.18) * mm});
            skPoint(sketch, "E94.visualSharp", {"position": v(-232.6, -91.18) * mm});
            skArc(sketch, "E94.filletArc", {"start": v(-232.6, -87.18) * mm, "mid": v(-231.43, -90) * mm, "end": v(-228.6, -91.18) * mm});
            skLineSegment(sketch, "E95", {"start": v(-114.3, -17.08) * mm, "end": v(-101.22, 18.97) * mm, "construction": true});
            skSolve(sketch);
        }
        {
            var Q0;
            Q0=qSketchRegion(id+"F12",true);
            var Q1;
            Q1=makeQuery(id+"F12.imprint","IMPRINT",FACE,{"disambiguationData":[TD([[makeQuery(id+"F12.imprint","IMPRINT",EDGE,{"derivedFrom":sQuery(id+"F12.wireOp",EDGE,"E51")}),-1.0]])]});
            var Q2;
            {var subQ1=sQuery(id+"F0.wireOp",EDGE,"E2");Q2=makeQuery(id+"F12.imprint","IMPRINT",FACE,{"disambiguationData":[TD([[makeQuery(id+"F12.imprint","IMPRINT",EDGE,{"derivedFrom":makeQuery(id+"F1.opExtrude","CAP_EDGE",EDGE,{"disambiguationData":[OSD([subQ1])],"isStart":false})}),1.0]])]});}
            extrude(context, id + "F13", {"entities" : qUnion([Q0, Q1, Q2]), "depth" : 6.7 * mm, "offsetDistance" : 25.4 * mm});
        }
        {
            var Q0;
            Q0=makeQuery(id+"F1.opExtrude","SWEPT_FACE",FACE,{"disambiguationData":[OSD([sQuery(id+"F0.wireOp",EDGE,"E0")])]});
            var sketch = newSketch(context, id + "F14", { "sketchPlane" : qUnion([Q0])});
            skLineSegment(sketch, "E96.bottom", {"start": v(0, 88.9) * mm, "end": v(-228.6, 88.9) * mm});
            skLineSegment(sketch, "E96.top", {"start": v(0, -88.9) * mm, "end": v(-228.6, -88.9) * mm});
            skLineSegment(sketch, "E96.left", {"start": v(-228.6, 88.9) * mm, "end": v(-228.6, -88.9) * mm});
            skLineSegment(sketch, "E96.right", {"start": v(0, 88.9) * mm, "end": v(0, -88.9) * mm});
            skCircle(sketch, "E97", {"center": v(-215.19, 54.5) * mm, "radius": 2.29 * mm});
            skCircle(sketch, "E98", {"center": v(-215.19, -64.67) * mm, "radius": 2.29 * mm});
            skCircle(sketch, "E99", {"center": v(-13.41, -64.67) * mm, "radius": 2.29 * mm});
            skCircle(sketch, "E100", {"center": v(-13.41, 54.5) * mm, "radius": 2.29 * mm});
            skLineSegment(sketch, "E101.0", {"start": v(-232.6, 88.9) * mm, "end": v(-232.6, -88.9) * mm});
            skLineSegment(sketch, "E101.1", {"start": v(0, 92.9) * mm, "end": v(-228.6, 92.9) * mm});
            skLineSegment(sketch, "E101.2", {"start": v(4, 88.9) * mm, "end": v(4, -88.9) * mm});
            skLineSegment(sketch, "E101.3", {"start": v(0, -92.9) * mm, "end": v(-228.6, -92.9) * mm});
            skPoint(sketch, "E102.visualSharp", {"position": v(-232.6, 92.9) * mm});
            skArc(sketch, "E102.filletArc", {"start": v(-228.6, 92.9) * mm, "mid": v(-231.43, 91.73) * mm, "end": v(-232.6, 88.9) * mm});
            skPoint(sketch, "E103.visualSharp", {"position": v(4, 92.9) * mm});
            skArc(sketch, "E103.filletArc", {"start": v(4, 88.9) * mm, "mid": v(2.83, 91.73) * mm, "end": v(0, 92.9) * mm});
            skPoint(sketch, "E104.visualSharp", {"position": v(4, -92.9) * mm});
            skArc(sketch, "E104.filletArc", {"start": v(0, -92.9) * mm, "mid": v(2.83, -91.73) * mm, "end": v(4, -88.9) * mm});
            skPoint(sketch, "E105.visualSharp", {"position": v(-232.6, -92.9) * mm});
            skArc(sketch, "E105.filletArc", {"start": v(-232.6, -88.9) * mm, "mid": v(-231.43, -91.73) * mm, "end": v(-228.6, -92.9) * mm});
            skSolve(sketch);
        }
        {
            var Q0;
            Q0=qSketchRegion(id+"F14",true);
            var Q1;
            {var subQ4=sQuery(id+"F14.wireOp",EDGE,"E96.bottom");Q1=makeQuery(id+"F14.imprint","IMPRINT",FACE,{"disambiguationData":[TD([[makeQuery(id+"F14.imprint","IMPRINT",EDGE,{"derivedFrom":subQ4}),1.0]])]});}
            var Q2;
            {var subQ1=sQuery(id+"F0.wireOp",EDGE,"E0");Q2=makeQuery(id+"F14.imprint","IMPRINT",FACE,{"disambiguationData":[TD([[makeQuery(id+"F14.imprint","IMPRINT",EDGE,{"derivedFrom":makeQuery(id+"F1.opExtrude","CAP_EDGE",EDGE,{"disambiguationData":[OSD([subQ1])],"isStart":false})}),1.0]])]});}
            extrude(context, id + "F15", {"entities" : qUnion([Q0, Q1, Q2]), "depth" : 6.7 * mm, "offsetDistance" : 25.4 * mm});
        }
        {
            var Q0;
            Q0=makeQuery(id+"F7.opExtrude","SWEPT_FACE",FACE,{"disambiguationData":[OSD([sQuery(id+"F0.wireOp",EDGE,"E1")])]});
            var sketch = newSketch(context, id + "F16", { "sketchPlane" : qUnion([Q0])});
            skCircle(sketch, "E106", {"center": v(35.51, 7.78) * mm, "radius": 12 * mm});
            skCircle(sketch, "E107", {"center": v(65.71, 7.78) * mm, "radius": 12 * mm});
            skCircle(sketch, "E108", {"center": v(193.09, 7.78) * mm, "radius": 12 * mm});
            skCircle(sketch, "E109", {"center": v(95.91, 7.78) * mm, "radius": 12 * mm});
            skCircle(sketch, "E110", {"center": v(35.51, 7.78) * mm, "radius": 13.6 * mm, "construction": true});
            skCircle(sketch, "E111", {"center": v(65.71, 7.78) * mm, "radius": 13.6 * mm, "construction": true});
            skCircle(sketch, "E112", {"center": v(95.91, 7.78) * mm, "radius": 13.6 * mm, "construction": true});
            skLineSegment(sketch, "E113.bottom", {"start": v(181.09, -1.72) * mm, "end": v(181.09, 17.28) * mm, "construction": true});
            skLineSegment(sketch, "E113.top", {"start": v(205.09, -1.72) * mm, "end": v(205.09, 17.28) * mm, "construction": true});
            skLineSegment(sketch, "E113.left", {"start": v(181.09, -1.72) * mm, "end": v(205.09, -1.72) * mm, "construction": true});
            skLineSegment(sketch, "E113.right", {"start": v(181.09, 17.28) * mm, "end": v(205.09, 17.28) * mm, "construction": true});
            skCircle(sketch, "E114", {"center": v(205.09, 17.28) * mm, "radius": 1.6 * mm});
            skCircle(sketch, "E115", {"center": v(181.09, -1.72) * mm, "radius": 1.6 * mm});
            skPoint(sketch, "E116", {"position": v(215.19, 7.78) * mm});
            skPoint(sketch, "E117", {"position": v(13.41, 7.78) * mm});
            skLineSegment(sketch, "E118", {"start": v(35.51, 7.78) * mm, "end": v(65.71, 7.78) * mm, "construction": true});
            skLineSegment(sketch, "E119", {"start": v(65.71, 7.78) * mm, "end": v(95.91, 7.78) * mm, "construction": true});
            skLineSegment(sketch, "E120", {"start": v(35.51, 7.78) * mm, "end": v(13.41, 7.78) * mm, "construction": true});
            skLineSegment(sketch, "E121", {"start": v(193.09, 7.78) * mm, "end": v(215.19, 7.78) * mm, "construction": true});
            skSolve(sketch);
        }
        {
            var Q0;
            Q0=makeQuery(id+"F16.imprint","IMPRINT",FACE,{"disambiguationData":[TD([[makeQuery(id+"F16.imprint","IMPRINT",EDGE,{"derivedFrom":sQuery(id+"F16.wireOp",EDGE,"E106")}),1.0]])]});
            var Q1;
            Q1=makeQuery(id+"F16.imprint","IMPRINT",FACE,{"disambiguationData":[TD([[makeQuery(id+"F16.imprint","IMPRINT",EDGE,{"derivedFrom":sQuery(id+"F16.wireOp",EDGE,"E107")}),1.0]])]});
            var Q2;
            Q2=makeQuery(id+"F16.imprint","IMPRINT",FACE,{"disambiguationData":[TD([[makeQuery(id+"F16.imprint","IMPRINT",EDGE,{"derivedFrom":sQuery(id+"F16.wireOp",EDGE,"E108")}),1.0]])]});
            var Q3;
            Q3=makeQuery(id+"F16.imprint","IMPRINT",FACE,{"disambiguationData":[TD([[makeQuery(id+"F16.imprint","IMPRINT",EDGE,{"derivedFrom":sQuery(id+"F16.wireOp",EDGE,"E109")}),1.0]])]});
            var Q4;
            Q4=makeQuery(id+"F16.imprint","IMPRINT",FACE,{"disambiguationData":[TD([[makeQuery(id+"F16.imprint","IMPRINT",EDGE,{"derivedFrom":sQuery(id+"F16.wireOp",EDGE,"B3YBxAYl-TvdG-dkWF-egrn-aJtRSMjf0zk2")}),1.0]])]});
            var Q5;
            Q5=makeQuery(id+"F16.imprint","IMPRINT",FACE,{"disambiguationData":[TD([[makeQuery(id+"F16.imprint","IMPRINT",EDGE,{"derivedFrom":sQuery(id+"F16.wireOp",EDGE,"E114")}),1.0]])]});
            var Q6;
            Q6=makeQuery(id+"F16.imprint","IMPRINT",FACE,{"disambiguationData":[TD([[makeQuery(id+"F16.imprint","IMPRINT",EDGE,{"derivedFrom":sQuery(id+"F16.wireOp",EDGE,"E115")}),1.0]])]});
            extrude(context, id + "F17", {"entities" : qUnion([Q0, Q1, Q2, Q3, Q4, Q5, Q6]), "operationType" : NewBodyOperationType.REMOVE, "endBound" : BoundingType.UP_TO_NEXT, "oppositeDirection" : true, "depth" : 25.4 * mm, "offsetDistance" : 25.4 * mm});
        }
    });
